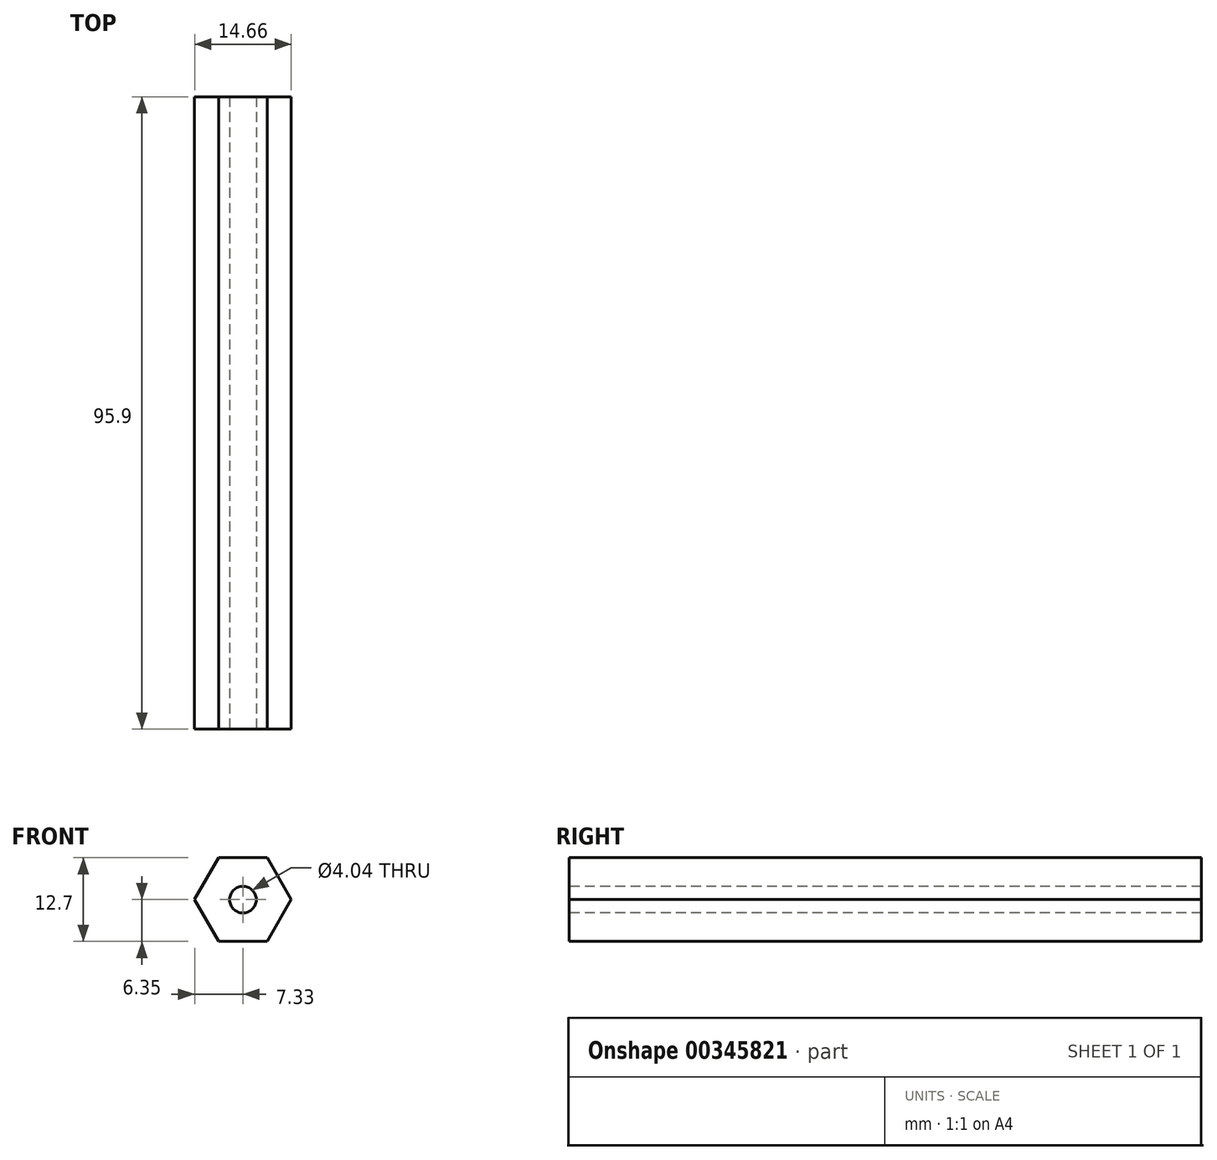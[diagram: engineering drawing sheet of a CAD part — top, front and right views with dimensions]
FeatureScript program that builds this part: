
annotation { "Feature Type Name" : "Feature", "Feature Type Description" : "" }
export const myFeature = defineFeature(function(context is Context, id is Id, definition is map)
    precondition{}
    {
        {
            var Q0;
            Q0=qCreatedBy(makeId("Front.planeOp"),FACE);
            var sketch = newSketch(context, id + "F0", { "sketchPlane" : qUnion([Q0])});
            skCircle(sketch, "E0.cCircle", {"center": v(0, 0) * mm, "radius": 6.35 * mm, "construction": true});
            skLineSegment(sketch, "E0.0", {"start": v(-3.67, 6.35) * mm, "end": v(3.67, 6.35) * mm});
            skLineSegment(sketch, "E0.1", {"start": v(3.67, 6.35) * mm, "end": v(7.33, 0) * mm});
            skLineSegment(sketch, "E0.2", {"start": v(7.33, 0) * mm, "end": v(3.67, -6.35) * mm});
            skLineSegment(sketch, "E0.3", {"start": v(3.67, -6.35) * mm, "end": v(-3.67, -6.35) * mm});
            skLineSegment(sketch, "E0.4", {"start": v(-3.67, -6.35) * mm, "end": v(-7.33, 0) * mm});
            skLineSegment(sketch, "E0.5", {"start": v(-7.33, 0) * mm, "end": v(-3.67, 6.35) * mm});
            skPoint(sketch, "E0.0.midPoint", {"position": v(0, 6.35) * mm});
            skSolve(sketch);
        }
        {
            var Q0;
            Q0 = qSketchRegion(id + "F0", true);
            extrude(context, id + "F1", {"entities" : qUnion([Q0]), "depth" : 95.9 * mm});
        }
        {
            var Q0;
            Q0=makeQuery(id+"F1.opExtrude","CAP_FACE",FACE,{"disambiguationData":[OSD([sQuery(id+"F0.wireOp",EDGE,"E0.0"),sQuery(id+"F0.wireOp",EDGE,"E0.1"),sQuery(id+"F0.wireOp",EDGE,"E0.2"),sQuery(id+"F0.wireOp",EDGE,"E0.3"),sQuery(id+"F0.wireOp",EDGE,"E0.4"),sQuery(id+"F0.wireOp",EDGE,"E0.5")])],"isStart":false});
            var sketch = newSketch(context, id + "F2", { "sketchPlane" : qUnion([Q0])});
            skPoint(sketch, "E1", {"position": v(0, 0) * mm});
            skSolve(sketch);
        }
        {
            var Q0;
            Q0=sQuery(id+"F2.wireOp",VERTEX,"E1");
            var Q1;
            Q1=makeQuery(id+"F1.opExtrude","SWEPT_BODY",BODY,{"disambiguationData":[OSD([sQuery(id+"F0.wireOp",EDGE,"E0.0"),sQuery(id+"F0.wireOp",EDGE,"E0.1"),sQuery(id+"F0.wireOp",EDGE,"E0.2"),sQuery(id+"F0.wireOp",EDGE,"E0.3"),sQuery(id+"F0.wireOp",EDGE,"E0.4"),sQuery(id+"F0.wireOp",EDGE,"E0.5")])]});
            hole(context, id + "F3", {"style" : HoleStyle.SIMPLE, "endStyle" : HoleEndStyle.THROUGH, "holeDiameter" : 4.04 * mm, "isTappedThrough" : true, "tappedDepth" : 12.7 * mm, "tapClearance" : 3, "locations" : qUnion([Q0]), "scope" : qUnion([Q1])});
        }
    });
